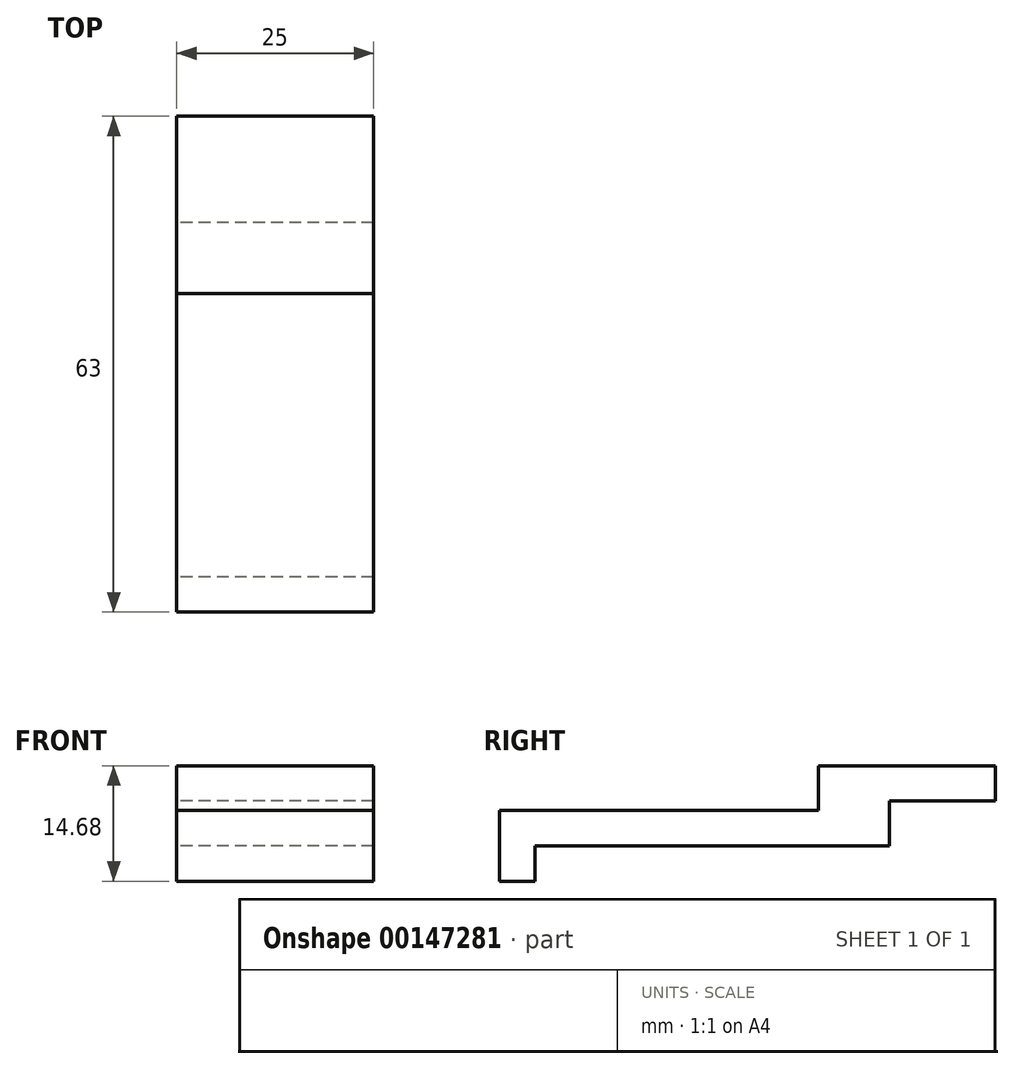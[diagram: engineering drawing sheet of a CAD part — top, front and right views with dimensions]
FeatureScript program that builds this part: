
annotation { "Feature Type Name" : "Feature", "Feature Type Description" : "" }
export const myFeature = defineFeature(function(context is Context, id is Id, definition is map)
    precondition{}
    {
        {
            var Q0;
            Q0=qCreatedBy(makeId("Right.planeOp"),FACE);
            var sketch = newSketch(context, id + "F0", { "sketchPlane" : qUnion([Q0])});
            skLineSegment(sketch, "E0", {"start": v(-45, 0) * mm, "end": v(0, 0) * mm});
            skLineSegment(sketch, "E1", {"start": v(-45, 0) * mm, "end": v(-45, -4.5) * mm});
            skLineSegment(sketch, "E2", {"start": v(-45, -4.5) * mm, "end": v(-49.5, -4.5) * mm});
            skLineSegment(sketch, "E3", {"start": v(-49.5, -4.5) * mm, "end": v(-49.5, 4.5) * mm});
            skLineSegment(sketch, "E4", {"start": v(-49.5, 4.5) * mm, "end": v(-9, 4.5) * mm});
            skLineSegment(sketch, "E5", {"start": v(-9, 4.5) * mm, "end": v(-9, 10.18) * mm});
            skLineSegment(sketch, "E6", {"start": v(-9, 10.18) * mm, "end": v(13.5, 10.18) * mm});
            skLineSegment(sketch, "E7", {"start": v(13.5, 10.18) * mm, "end": v(13.5, 5.68) * mm});
            skLineSegment(sketch, "E8", {"start": v(13.5, 5.68) * mm, "end": v(0, 5.68) * mm});
            skLineSegment(sketch, "E9", {"start": v(0, 5.68) * mm, "end": v(0, 0) * mm});
            skSolve(sketch);
        }
        {
            var Q0;
            Q0 = qSketchRegion(id + "F0", true);
            extrude(context, id + "F1", {"entities" : qUnion([Q0]), "depth" : 25 * mm});
        }
    });
